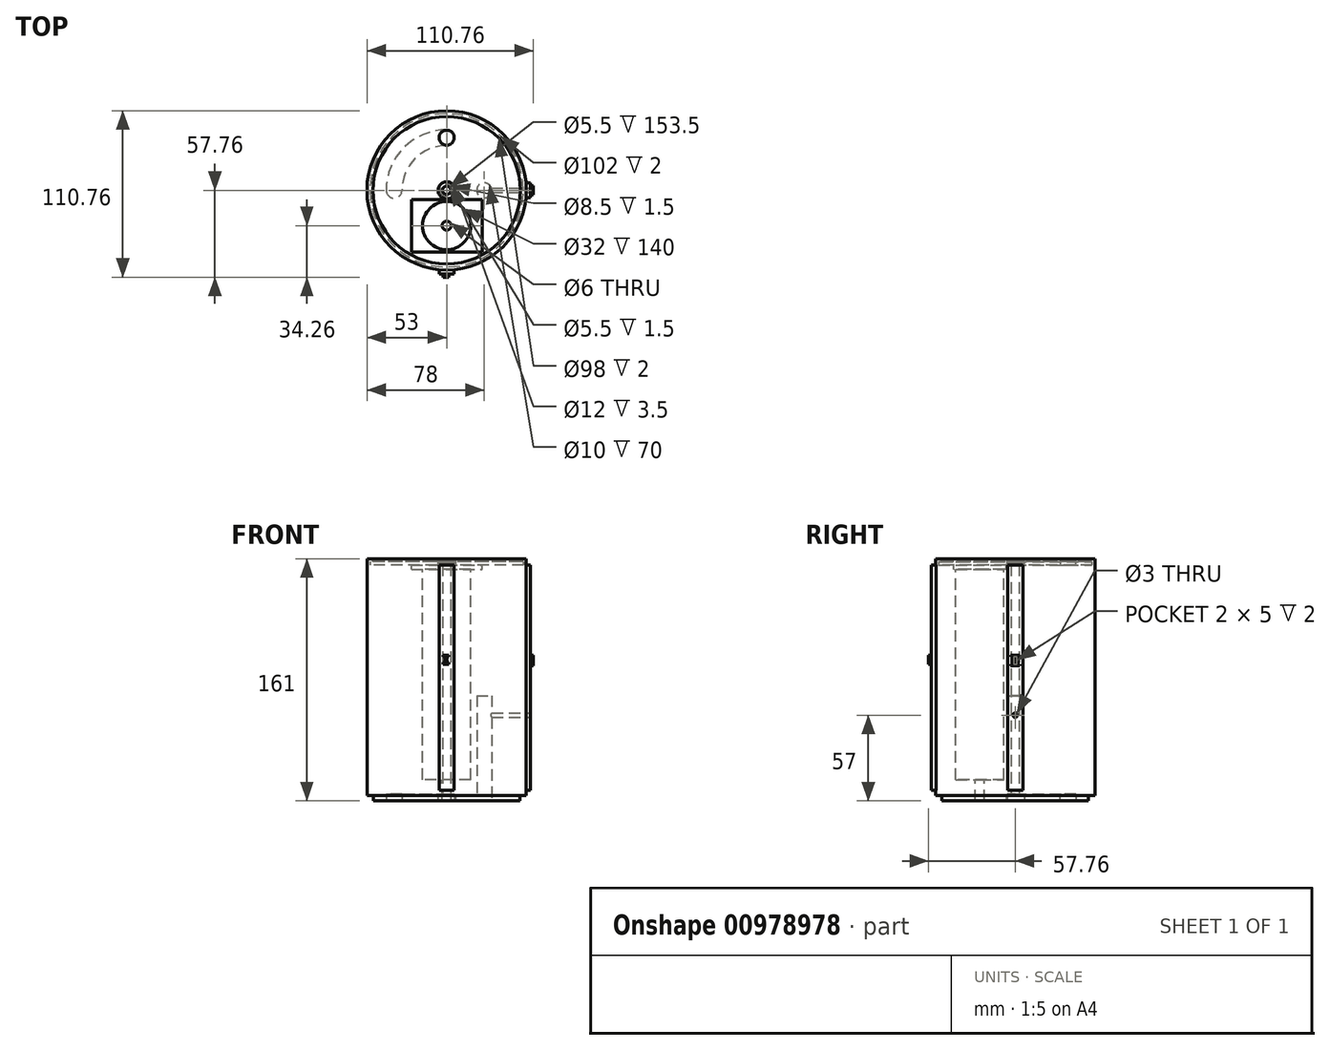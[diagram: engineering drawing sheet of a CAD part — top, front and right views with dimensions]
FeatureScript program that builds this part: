
annotation { "Feature Type Name" : "Feature", "Feature Type Description" : "" }
export const myFeature = defineFeature(function(context is Context, id is Id, definition is map)
    precondition{}
    {
        {
            var Q0;
            Q0=qCreatedBy(makeId("Top.planeOp"),FACE);
            var sketch = newSketch(context, id + "F0", { "sketchPlane" : qUnion([Q0])});
            skCircle(sketch, "E0", {"center": v(0, 0) * mm, "radius": 53 * mm});
            skCircle(sketch, "E1", {"center": v(0, 0) * mm, "radius": 2.75 * mm});
            skSolve(sketch);
        }
        {
            var Q0;
            Q0=makeQuery(id+"F0.imprint","IMPRINT",FACE,{"disambiguationData":[TD([[makeQuery(id+"F0.imprint","IMPRINT",EDGE,{"derivedFrom":sQuery(id+"F0.wireOp",EDGE,"E0")}),1.0]])]});
            extrude(context, id + "F1", {"entities" : qUnion([Q0]), "depth" : 157 * mm, "offsetDistance" : 25 * mm});
        }
        {
            var Q0;
            Q0=makeQuery(id+"F1.opExtrude","CAP_FACE",FACE,{"disambiguationData":[OSD([sQuery(id+"F0.wireOp",EDGE,"E0"),sQuery(id+"F0.wireOp",EDGE,"E1")])],"isStart":false});
            var sketch = newSketch(context, id + "F2", { "sketchPlane" : qUnion([Q0])});
            skLineSegment(sketch, "E2.bottom", {"start": v(-23.5, -6) * mm, "end": v(23.5, -6) * mm});
            skLineSegment(sketch, "E2.top", {"start": v(-23.5, -41) * mm, "end": v(23.5, -41) * mm});
            skLineSegment(sketch, "E2.left", {"start": v(-23.5, -6) * mm, "end": v(-23.5, -41) * mm});
            skLineSegment(sketch, "E2.right", {"start": v(23.5, -6) * mm, "end": v(23.5, -41) * mm});
            skCircle(sketch, "E3", {"center": v(0, 0) * mm, "radius": 5.75 * mm});
            skCircle(sketch, "E4", {"center": v(0, 0) * mm, "radius": 4.25 * mm});
            skCircle(sketch, "E5", {"center": v(0, 0) * mm, "radius": 51 * mm});
            skCircle(sketch, "E6", {"center": v(0, 35) * mm, "radius": 5 * mm});
            skLineSegment(sketch, "E7", {"start": v(52.76, 5) * mm, "end": v(55.76, 5) * mm});
            skLineSegment(sketch, "E8", {"start": v(55.76, 5) * mm, "end": v(55.76, -5) * mm});
            skLineSegment(sketch, "E9", {"start": v(55.76, -5) * mm, "end": v(52.76, -5) * mm});
            skLineSegment(sketch, "E10", {"start": v(-5, -52.76) * mm, "end": v(-5, -55.76) * mm});
            skLineSegment(sketch, "E11", {"start": v(-5, -55.76) * mm, "end": v(5, -55.76) * mm});
            skLineSegment(sketch, "E12", {"start": v(5, -55.76) * mm, "end": v(5, -52.76) * mm});
            skSolve(sketch);
        }
        {
            var Q0;
            Q0=makeQuery(id+"F2.imprint","IMPRINT",FACE,{"disambiguationData":[TD([[makeQuery(id+"F2.imprint","IMPRINT",EDGE,{"derivedFrom":sQuery(id+"F2.wireOp",EDGE,"E2.bottom")}),-1.0]])]});
            extrude(context, id + "F3", {"entities" : qUnion([Q0]), "operationType" : NewBodyOperationType.REMOVE, "oppositeDirection" : true, "depth" : 3 * mm, "offsetDistance" : 25 * mm});
        }
        {
            var Q0;
            Q0=makeQuery(id+"F3.boolean.opBoolean","COPY",FACE,{"derivedFrom":makeQuery(id+"F3.opExtrude","CAP_FACE",FACE,{"disambiguationData":[OSD([sQuery(id+"F2.wireOp",EDGE,"E2.bottom"),sQuery(id+"F2.wireOp",EDGE,"E2.top"),sQuery(id+"F2.wireOp",EDGE,"E2.left"),sQuery(id+"F2.wireOp",EDGE,"E2.right")])],"isStart":false})});
            var sketch = newSketch(context, id + "F4", { "sketchPlane" : qUnion([Q0])});
            skCircle(sketch, "E13", {"center": v(0, -23.5) * mm, "radius": 16 * mm});
            skSolve(sketch);
        }
        {
            var Q0;
            Q0=makeQuery(id+"F4.imprint","IMPRINT",FACE,{"disambiguationData":[TD([[makeQuery(id+"F4.imprint","IMPRINT",EDGE,{"derivedFrom":sQuery(id+"F4.wireOp",EDGE,"E13")}),1.0]])]});
            extrude(context, id + "F5", {"entities" : qUnion([Q0]), "operationType" : NewBodyOperationType.REMOVE, "oppositeDirection" : true, "depth" : 140 * mm, "offsetDistance" : 25 * mm});
        }
        {
            var Q0;
            Q0=makeQuery(id+"F5.boolean.opBoolean","COPY",FACE,{"derivedFrom":makeQuery(id+"F5.opExtrude","CAP_FACE",FACE,{"disambiguationData":[OSD([sQuery(id+"F4.wireOp",EDGE,"E13")])],"isStart":false})});
            var sketch = newSketch(context, id + "F6", { "sketchPlane" : qUnion([Q0])});
            skCircle(sketch, "E14", {"center": v(0, -23.5) * mm, "radius": 3 * mm});
            skSolve(sketch);
        }
        {
            var Q0;
            Q0=makeQuery(id+"F6.imprint","IMPRINT",FACE,{"disambiguationData":[TD([[makeQuery(id+"F6.imprint","IMPRINT",EDGE,{"derivedFrom":sQuery(id+"F6.wireOp",EDGE,"E14")}),1.0]])]});
            extrude(context, id + "F7", {"entities" : qUnion([Q0]), "operationType" : NewBodyOperationType.REMOVE, "oppositeDirection" : true, "depth" : 14 * mm, "offsetDistance" : 25 * mm});
        }
        {
            var Q0;
            Q0=makeQuery(id+"F2.imprint","IMPRINT",FACE,{"disambiguationData":[TD([[makeQuery(id+"F2.imprint","IMPRINT",EDGE,{"derivedFrom":sQuery(id+"F2.wireOp",EDGE,"E3")}),1.0]])]});
            extrude(context, id + "F8", {"entities" : qUnion([Q0]), "operationType" : NewBodyOperationType.ADD, "depth" : 3 * mm, "offsetDistance" : 25 * mm});
        }
        {
            var Q0;
            Q0=makeQuery(id+"F8.opExtrude","CAP_FACE",FACE,{"disambiguationData":[OSD([sQuery(id+"F2.wireOp",EDGE,"E3"),sQuery(id+"F2.wireOp",EDGE,"E4")])],"isStart":false});
            var sketch = newSketch(context, id + "F9", { "sketchPlane" : qUnion([Q0])});
            skCircle(sketch, "E15", {"center": v(0, 0) * mm, "radius": 2.75 * mm});
            skSolve(sketch);
        }
        {
            var Q0;
            Q0=makeQuery(id+"F9.imprint","IMPRINT",FACE,{"disambiguationData":[TD([[makeQuery(id+"F9.imprint","IMPRINT",EDGE,{"derivedFrom":sQuery(id+"F9.wireOp",EDGE,"E15")}),-1.0]])]});
            extrude(context, id + "F10", {"entities" : qUnion([Q0]), "operationType" : NewBodyOperationType.ADD, "oppositeDirection" : true, "depth" : 1.5 * mm, "offsetDistance" : 25 * mm});
        }
        {
            var Q0;
            Q0=makeQuery(id+"F2.imprint","IMPRINT",FACE,{"disambiguationData":[TD([[makeQuery(id+"F2.imprint","IMPRINT",EDGE,{"derivedFrom":sQuery(id+"F2.wireOp",EDGE,"E5")}),-1.0]])]});
            extrude(context, id + "F11", {"entities" : qUnion([Q0]), "operationType" : NewBodyOperationType.ADD, "depth" : 4 * mm, "offsetDistance" : 25 * mm});
        }
        {
            var Q0;
            Q0=makeQuery(id+"F11.opExtrude","CAP_FACE",FACE,{"disambiguationData":[OSD([sQuery(id+"F0.wireOp",EDGE,"E0"),sQuery(id+"F2.wireOp",EDGE,"E5")])],"isStart":false});
            var sketch = newSketch(context, id + "F12", { "sketchPlane" : qUnion([Q0])});
            skCircle(sketch, "E16", {"center": v(0, 0) * mm, "radius": 49 * mm});
            skSolve(sketch);
        }
        {
            var Q0;
            Q0=makeQuery(id+"F12.imprint","IMPRINT",FACE,{"disambiguationData":[TD([[makeQuery(id+"F12.imprint","IMPRINT",EDGE,{"derivedFrom":sQuery(id+"F12.wireOp",EDGE,"E16")}),-1.0]])]});
            extrude(context, id + "F13", {"entities" : qUnion([Q0]), "operationType" : NewBodyOperationType.ADD, "oppositeDirection" : true, "depth" : 2 * mm, "offsetDistance" : 25 * mm});
        }
        {
            var Q0;
            Q0=makeQuery(id+"F1.opExtrude","CAP_FACE",FACE,{"disambiguationData":[OSD([sQuery(id+"F0.wireOp",EDGE,"E0"),sQuery(id+"F0.wireOp",EDGE,"E1")])],"isStart":true});
            var sketch = newSketch(context, id + "F14", { "sketchPlane" : qUnion([Q0])});
            skCircle(sketch, "E17", {"center": v(0, 0) * mm, "radius": 48.75 * mm});
            skCircle(sketch, "E18", {"center": v(0, 0) * mm, "radius": 6 * mm});
            skCircle(sketch, "E19", {"center": v(25, 0) * mm, "radius": 5 * mm});
            skCircle(sketch, "E20", {"center": v(0, -35) * mm, "radius": 5.25 * mm});
            skCircle(sketch, "E21", {"center": v(-35, 0) * mm, "radius": 5.25 * mm});
            skCircle(sketch, "E22", {"center": v(0, 0) * mm, "radius": 29.75 * mm});
            skCircle(sketch, "E23", {"center": v(0, 0) * mm, "radius": 40.25 * mm});
            skSolve(sketch);
        }
        {
            var Q0;
            Q0=makeQuery(id+"F14.imprint","IMPRINT",FACE,{"disambiguationData":[TD([[makeQuery(id+"F14.imprint","IMPRINT",EDGE,{"derivedFrom":sQuery(id+"F14.wireOp",EDGE,"E17")}),-1.0]])]});
            var Q1;
            Q1=makeQuery(id+"F14.imprint","IMPRINT",FACE,{"disambiguationData":[TD([[makeQuery(id+"F14.imprint","IMPRINT",EDGE,{"derivedFrom":sQuery(id+"F14.wireOp",EDGE,"E18")}),1.0]])]});
            extrude(context, id + "F15", {"entities" : qUnion([Q0, Q1]), "operationType" : NewBodyOperationType.REMOVE, "oppositeDirection" : true, "depth" : 3.5 * mm, "offsetDistance" : 25 * mm});
        }
        {
            var Q0;
            Q0=makeQuery(id+"F2.imprint","IMPRINT",FACE,{"disambiguationData":[TD([[makeQuery(id+"F2.imprint","IMPRINT",EDGE,{"derivedFrom":sQuery(id+"F2.wireOp",EDGE,"E6")}),1.0]])]});
            extrude(context, id + "F16", {"entities" : qUnion([Q0]), "operationType" : NewBodyOperationType.ADD, "depth" : 4 * mm, "offsetDistance" : 25 * mm});
        }
        {
            var Q0;
            {var subQ0=sQuery(id+"F2.wireOp",EDGE,"E7");Q0=makeQuery(id+"F2.imprint","IMPRINT",FACE,{"disambiguationData":[TD([[makeQuery(id+"F2.imprint","IMPRINT",EDGE,{"derivedFrom":subQ0}),-1.0]])]});}
            extrude(context, id + "F17", {"entities" : qUnion([Q0]), "operationType" : NewBodyOperationType.ADD, "oppositeDirection" : true, "depth" : 150 * mm, "offsetDistance" : 25 * mm});
        }
        {
            var Q0;
            Q0=makeQuery(id+"F14.imprint","IMPRINT",FACE,{"disambiguationData":[TD([[makeQuery(id+"F14.imprint","IMPRINT",EDGE,{"derivedFrom":sQuery(id+"F14.wireOp",EDGE,"E19")}),1.0]])]});
            var Q1;
            {var subQ0=sQuery(id+"F14.wireOp",EDGE,"E22");var subQ1=sQuery(id+"F14.wireOp",EDGE,"E19");var subQ2=makeQuery(id+"F14.imprint","INTERSECT",VERTEX,{"disambiguationData":[OD(0.0)],"derivedFrom":[subQ1,subQ0]});Q1=makeQuery(id+"F14.imprint","IMPRINT",FACE,{"disambiguationData":[TD([[makeQuery(id+"F14.imprint","IMPRINT",EDGE,{"disambiguationData":[TD([[subQ2,-1.0]])],"derivedFrom":subQ1}),1.0]])]});}
            var Q2;
            {var subQ0=sQuery(id+"F14.wireOp",EDGE,"E23");var subQ1=sQuery(id+"F14.wireOp",EDGE,"E19");var subQ2=makeQuery(id+"F14.imprint","INTERSECT",VERTEX,{"disambiguationData":[OD(0.0)],"derivedFrom":[subQ1,subQ0]});Q2=makeQuery(id+"F14.imprint","IMPRINT",FACE,{"disambiguationData":[TD([[makeQuery(id+"F14.imprint","IMPRINT",EDGE,{"disambiguationData":[TD([[subQ2,1.0]])],"derivedFrom":subQ1}),1.0]])]});}
            extrude(context, id + "F18", {"entities" : qUnion([Q0, Q1, Q2]), "operationType" : NewBodyOperationType.REMOVE, "oppositeDirection" : true, "depth" : 70 * mm, "offsetDistance" : 25 * mm});
        }
        {
            var Q0;
            Q0=makeQuery(id+"F17.opExtrude","SWEPT_FACE",FACE,{"disambiguationData":[OSD([sQuery(id+"F2.wireOp",EDGE,"E8")])]});
            var sketch = newSketch(context, id + "F19", { "sketchPlane" : qUnion([Q0])});
            skCircle(sketch, "E24", {"center": v(0, 57) * mm, "radius": 1.5 * mm});
            skLineSegment(sketch, "E25", {"start": v(-3, 97) * mm, "end": v(3, 97) * mm});
            skLineSegment(sketch, "E26", {"start": v(3, 97) * mm, "end": v(3, 96) * mm});
            skLineSegment(sketch, "E27", {"start": v(3, 96) * mm, "end": v(2, 96) * mm});
            skLineSegment(sketch, "E28", {"start": v(2, 96) * mm, "end": v(2, 91) * mm});
            skLineSegment(sketch, "E29", {"start": v(2, 91) * mm, "end": v(3, 91) * mm});
            skLineSegment(sketch, "E30", {"start": v(3, 91) * mm, "end": v(3, 90) * mm});
            skLineSegment(sketch, "E31", {"start": v(3, 90) * mm, "end": v(-3, 90) * mm});
            skLineSegment(sketch, "E32", {"start": v(-3, 90) * mm, "end": v(-3, 91) * mm});
            skLineSegment(sketch, "E33", {"start": v(-3, 91) * mm, "end": v(-2, 91) * mm});
            skLineSegment(sketch, "E34", {"start": v(-2, 91) * mm, "end": v(-2, 96) * mm});
            skLineSegment(sketch, "E35", {"start": v(-2, 96) * mm, "end": v(-3, 96) * mm});
            skLineSegment(sketch, "E36", {"start": v(-3, 96) * mm, "end": v(-3, 97) * mm});
            skLineSegment(sketch, "E37", {"start": v(-1, 96) * mm, "end": v(1, 96) * mm});
            skLineSegment(sketch, "E38", {"start": v(1, 96) * mm, "end": v(1, 91) * mm});
            skLineSegment(sketch, "E39", {"start": v(1, 91) * mm, "end": v(-1, 91) * mm});
            skLineSegment(sketch, "E40", {"start": v(-1, 91) * mm, "end": v(-1, 96) * mm});
            skSolve(sketch);
        }
        {
            var Q0;
            Q0=makeQuery(id+"F19.imprint","IMPRINT",FACE,{"disambiguationData":[TD([[makeQuery(id+"F19.imprint","IMPRINT",EDGE,{"derivedFrom":sQuery(id+"F19.wireOp",EDGE,"E24")}),1.0]])]});
            extrude(context, id + "F20", {"entities" : qUnion([Q0]), "operationType" : NewBodyOperationType.REMOVE, "oppositeDirection" : true, "depth" : 30 * mm, "offsetDistance" : 25 * mm});
        }
        {
            var Q0;
            {var subQ0=sQuery(id+"F2.wireOp",EDGE,"E10");Q0=makeQuery(id+"F2.imprint","IMPRINT",FACE,{"disambiguationData":[TD([[makeQuery(id+"F2.imprint","IMPRINT",EDGE,{"derivedFrom":subQ0}),1.0]])]});}
            extrude(context, id + "F21", {"entities" : qUnion([Q0]), "operationType" : NewBodyOperationType.ADD, "oppositeDirection" : true, "depth" : 150 * mm, "offsetDistance" : 25 * mm});
        }
        {
            var Q0;
            {var subQ0=sQuery(id+"F14.wireOp",EDGE,"E21");var subQ1=makeQuery(id+"F14.imprint","INTERSECT",VERTEX,{"derivedFrom":[subQ0,sQuery(id+"F14.wireOp",EDGE,"E22")]});Q0=makeQuery(id+"F14.imprint","IMPRINT",FACE,{"disambiguationData":[TD([[makeQuery(id+"F14.imprint","IMPRINT",EDGE,{"disambiguationData":[TD([[subQ1,-1.0]])],"derivedFrom":subQ0}),1.0]])]});}
            var Q1;
            {var subQ0=sQuery(id+"F14.wireOp",EDGE,"E22");var subQ1=sQuery(id+"F14.wireOp",EDGE,"E20");var subQ2=makeQuery(id+"F14.imprint","INTERSECT",VERTEX,{"derivedFrom":[subQ1,subQ0]});Q1=makeQuery(id+"F14.imprint","IMPRINT",FACE,{"disambiguationData":[TD([[makeQuery(id+"F14.imprint","IMPRINT",EDGE,{"disambiguationData":[TD([[subQ2,-1.0]])],"derivedFrom":subQ1}),-1.0]])]});}
            var Q2;
            {var subQ0=sQuery(id+"F14.wireOp",EDGE,"E20");var subQ1=makeQuery(id+"F14.imprint","INTERSECT",VERTEX,{"derivedFrom":[subQ0,sQuery(id+"F14.wireOp",EDGE,"E22")]});Q2=makeQuery(id+"F14.imprint","IMPRINT",FACE,{"disambiguationData":[TD([[makeQuery(id+"F14.imprint","IMPRINT",EDGE,{"disambiguationData":[TD([[subQ1,-1.0]])],"derivedFrom":subQ0}),1.0]])]});}
            extrude(context, id + "F22", {"entities" : qUnion([Q0, Q1, Q2]), "operationType" : NewBodyOperationType.REMOVE, "oppositeDirection" : true, "depth" : 4.5 * mm, "offsetDistance" : 25 * mm});
        }
        {
            var Q0;
            Q0=makeQuery(id+"F19.imprint","IMPRINT",FACE,{"disambiguationData":[TD([[makeQuery(id+"F19.imprint","IMPRINT",EDGE,{"derivedFrom":sQuery(id+"F19.wireOp",EDGE,"E25")}),-1.0]])]});
            extrude(context, id + "F23", {"entities" : qUnion([Q0]), "operationType" : NewBodyOperationType.ADD, "depth" : 2 * mm, "offsetDistance" : 25 * mm});
        }
        {
            var Q0;
            Q0=makeQuery(id+"F21.opExtrude","SWEPT_FACE",FACE,{"disambiguationData":[OSD([sQuery(id+"F2.wireOp",EDGE,"E11")])]});
            var sketch = newSketch(context, id + "F24", { "sketchPlane" : qUnion([Q0])});
            skLineSegment(sketch, "E41", {"start": v(-2.5, 97) * mm, "end": v(1.5, 97) * mm});
            skLineSegment(sketch, "E42", {"start": v(1.5, 97) * mm, "end": v(1.5, 96) * mm});
            skLineSegment(sketch, "E43", {"start": v(1.5, 96) * mm, "end": v(0, 96) * mm});
            skLineSegment(sketch, "E44", {"start": v(0, 96) * mm, "end": v(0, 92) * mm});
            skLineSegment(sketch, "E45", {"start": v(0, 92) * mm, "end": v(1.5, 92) * mm});
            skLineSegment(sketch, "E46", {"start": v(1.5, 92) * mm, "end": v(1.5, 91) * mm});
            skLineSegment(sketch, "E47", {"start": v(1.5, 91) * mm, "end": v(-2.5, 91) * mm});
            skLineSegment(sketch, "E48", {"start": v(-2.5, 91) * mm, "end": v(-2.5, 92) * mm});
            skLineSegment(sketch, "E49", {"start": v(-2.5, 92) * mm, "end": v(-1, 92) * mm});
            skLineSegment(sketch, "E50", {"start": v(-1, 92) * mm, "end": v(-1, 96) * mm});
            skLineSegment(sketch, "E51", {"start": v(-1, 96) * mm, "end": v(-2.5, 96) * mm});
            skLineSegment(sketch, "E52", {"start": v(-2.5, 96) * mm, "end": v(-2.5, 97) * mm});
            skSolve(sketch);
        }
        {
            var Q0;
            Q0=makeQuery(id+"F24.imprint","IMPRINT",FACE,{"disambiguationData":[TD([[makeQuery(id+"F24.imprint","IMPRINT",EDGE,{"derivedFrom":sQuery(id+"F24.wireOp",EDGE,"E41")}),-1.0]])]});
            extrude(context, id + "F25", {"entities" : qUnion([Q0]), "operationType" : NewBodyOperationType.ADD, "depth" : 2 * mm, "offsetDistance" : 25 * mm});
        }
    });
